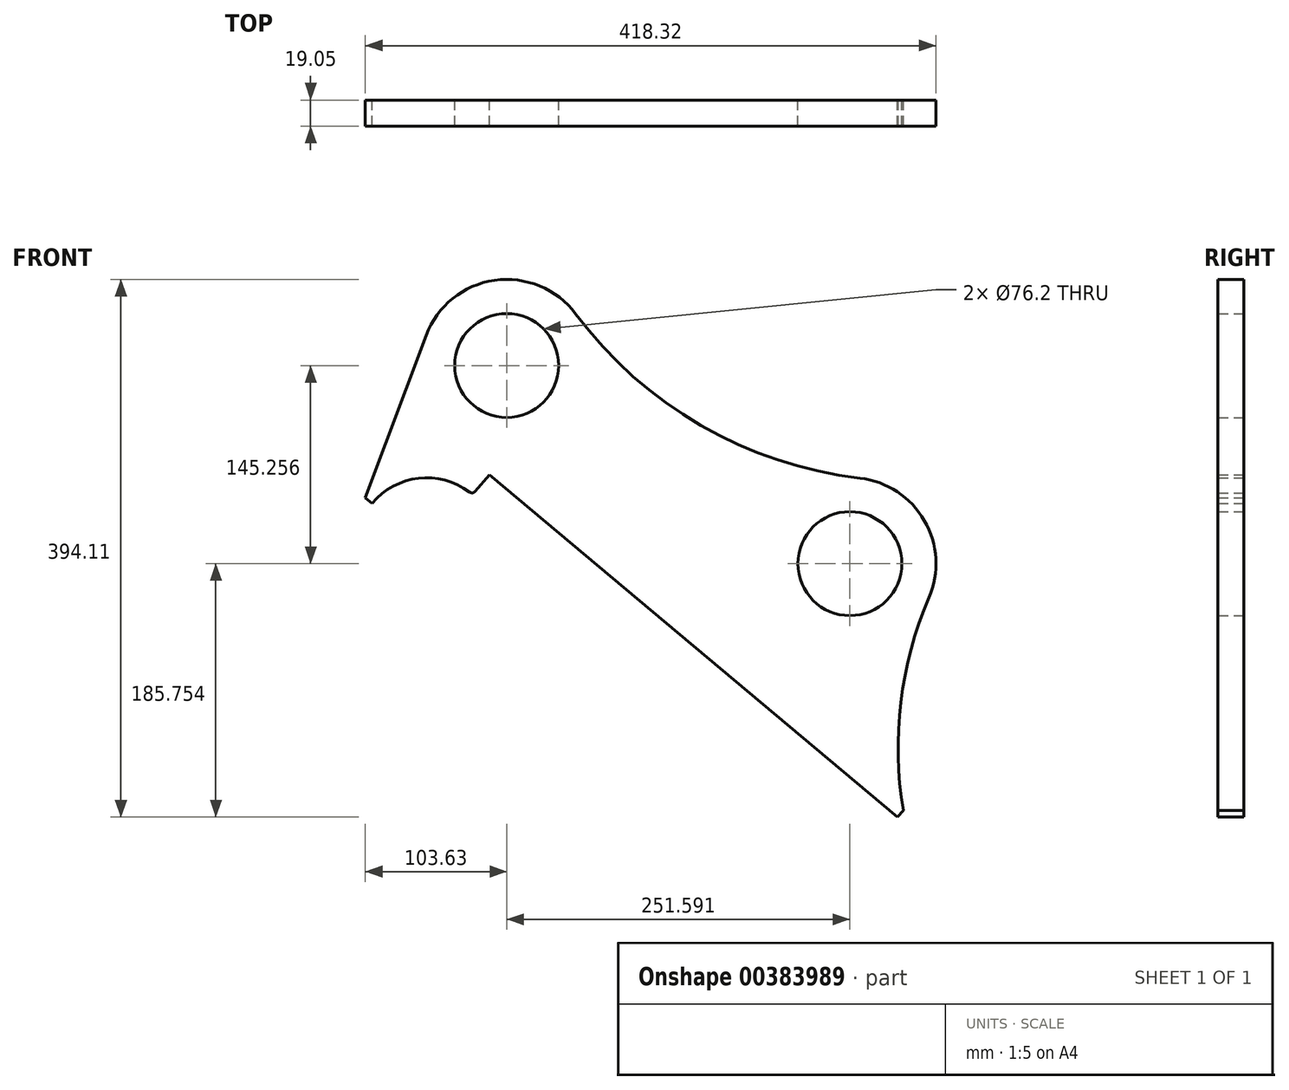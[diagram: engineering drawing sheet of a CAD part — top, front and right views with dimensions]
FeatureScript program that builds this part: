
annotation { "Feature Type Name" : "Feature", "Feature Type Description" : "" }
export const myFeature = defineFeature(function(context is Context, id is Id, definition is map)
    precondition{}
    {
        {
            var Q0;
            Q0=qCreatedBy(makeId("Front.planeOp"),FACE);
            var sketch = newSketch(context, id + "F0", { "sketchPlane" : qUnion([Q0])});
            skLineSegment(sketch, "E0", {"start": v(0, 0) * mm, "end": v(268.7, 0) * mm, "construction": true});
            skLineSegment(sketch, "E1", {"start": v(0, 0) * mm, "end": v(346, -199.77) * mm, "construction": true});
            skLineSegment(sketch, "E2", {"start": v(0, 0) * mm, "end": v(296.53, -248.82) * mm, "construction": true});
            skSolve(sketch);
        }
        {
            var Q0;
            Q0=qCreatedBy(makeId("Front.planeOp"),FACE);
            var sketch = newSketch(context, id + "F1", { "sketchPlane" : qUnion([Q0])});
            skCircle(sketch, "E3", {"center": v(0, 0) * mm, "radius": 38.1 * mm});
            skCircle(sketch, "E4", {"center": v(0, 0) * mm, "radius": 63.1 * mm});
            skCircle(sketch, "E5", {"center": v(251.6, -145.26) * mm, "radius": 63.1 * mm});
            skCircle(sketch, "E6", {"center": v(251.6, -145.26) * mm, "radius": 38.1 * mm});
            skArc(sketch, "E7", {"start": v(50.56, 37.75) * mm, "mid": v(142.4, -43.87) * mm, "end": v(259, -82.6) * mm});
            skLineSegment(sketch, "E8", {"start": v(-22.98, -92.22) * mm, "end": v(-12.72, -79.99) * mm});
            skLineSegment(sketch, "E9", {"start": v(286.44, -331.01) * mm, "end": v(-12.72, -79.99) * mm});
            skLineSegment(sketch, "E10", {"start": v(-24.96, -94.58) * mm, "end": v(-65.1, -60.9) * mm, "construction": true});
            skLineSegment(sketch, "E11", {"start": v(-65.1, -60.9) * mm, "end": v(-98.77, -101.04) * mm, "construction": true});
            skArc(sketch, "E12", {"start": v(-27.31, -92.72) * mm, "mid": v(-64.7, -82.68) * mm, "end": v(-98.77, -101.04) * mm});
            skLineSegment(sketch, "E13", {"start": v(-48.34, 40.56) * mm, "end": v(-166.75, -100.55) * mm, "construction": true});
            skLineSegment(sketch, "E14", {"start": v(-166.75, -100.55) * mm, "end": v(229.84, -433.33) * mm, "construction": true});
            skLineSegment(sketch, "E15", {"start": v(286.44, -331.01) * mm, "end": v(290.74, -326.34) * mm});
            skArc(sketch, "E16", {"start": v(309.58, -170.14) * mm, "mid": v(288.94, -246.89) * mm, "end": v(290.74, -326.34) * mm});
            skLineSegment(sketch, "E17", {"start": v(-98.77, -101.04) * mm, "end": v(-103.63, -96.96) * mm});
            skLineSegment(sketch, "E18", {"start": v(-103.63, -96.96) * mm, "end": v(-59.1, 22.1) * mm});
            skPoint(sketch, "E19.visualSharp", {"position": v(-24.96, -94.58) * mm});
            skArc(sketch, "E19.filletArc", {"start": v(-27.31, -92.72) * mm, "mid": v(-25.04, -93.33) * mm, "end": v(-22.98, -92.22) * mm});
            skSolve(sketch);
        }
        {
            var Q0;
            Q0=makeQuery(id+"F1.imprint","IMPRINT",FACE,{"disambiguationData":[TD([[makeQuery(id+"F1.imprint","IMPRINT",EDGE,{"derivedFrom":sQuery(id+"F1.wireOp",EDGE,"E3")}),-1.0]])]});
            var Q1;
            {var subQ2=sQuery(id+"F1.wireOp",EDGE,"E7");Q1=makeQuery(id+"F1.imprint","IMPRINT",FACE,{"disambiguationData":[TD([[makeQuery(id+"F1.imprint","IMPRINT",EDGE,{"derivedFrom":subQ2}),-1.0]])]});}
            var Q2;
            Q2=makeQuery(id+"F1.imprint","IMPRINT",FACE,{"disambiguationData":[TD([[makeQuery(id+"F1.imprint","IMPRINT",EDGE,{"derivedFrom":sQuery(id+"F1.wireOp",EDGE,"E6")}),-1.0]])]});
            extrude(context, id + "F2", {"entities" : qUnion([Q0, Q1, Q2]), "depth" : 19.05 * mm, "offsetDistance" : 25.4 * mm});
        }
    });
